SOLIDWORKS PART (.sldprt)
format: sldprt  version: not decoded by parser v0  size: 250,368 bytes
history: native  units: mm
features: plane x3, sketch x2, material x1, extrude x1, fillet x1, cut_extrude x1 (+7 scaffold rows collapsed)
feature tree (16):
  scaffold x7  (default folders/planes/origin — collapsed)
  material  "材质 <未指定>"
  plane  "前视基准面"
  plane  "上视基准面"
  plane  "右视基准面"
  sketch  "草图1"  dims[D1=130.0mm D2=130.0mm]
  extrude  "凸台-拉伸1"  Depth=3mm
  fillet  "圆角1"  Radius=35mm
  sketch  "草图5"  dims[D1=0.0mm D2=0.0mm D3=0.0mm D4=0.0mm D5=0.0mm D6=0.0mm D7=0.0mm D8=0.0mm D9=0.0mm D10=0.0mm D11=0.0mm D12=0.0mm D13=0.0mm D14=0.0mm D15=0.0mm D16=0.0mm D17=0.0mm D18=0.0mm D19=0.0mm D20=0.0mm D21=0.0mm D22=0.0mm D23=0.0mm D24=0.0mm D25=0.0mm D26=0.0mm D27=0.0mm D28=0.0mm D29=0.0mm D30=0.0mm D31=0.0mm D32=0.0mm D33=0.0mm D34=0.0mm D35=0.0mm D36=0.0mm D37=0.0mm D38=0.0mm D39=0.0mm D40=0.0mm D41=0.0mm D42=0.0mm D43=0.0mm D44=0.0mm D45=0.0mm D46=0.0mm D47=0.0mm D48=0.0mm D49=0.0mm D50=0.0mm]
  cut_extrude  "切除-拉伸2"  Depth=13mm
decode coverage: 5 of 5 modeling features carry decoded parameters
note: suppression state not decoded; provenance and decode notes live in map.json
